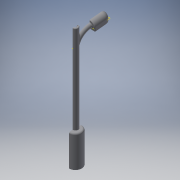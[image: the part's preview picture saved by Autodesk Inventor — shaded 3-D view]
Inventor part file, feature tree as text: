
AUTODESK INVENTOR PART (.ipt)
format: ipt  version: 2018 (Build 220112000, 112)  size: 398,336 bytes
history: native  units: in
note: dims shown in document units (in); Inventor stores cm internally (conversion verified against a paired STEP export)
features: sketch x10, other x3, plane x1
ambient origin geometry x8: Origin, YZ Plane, XZ Plane, XY Plane, X Axis, Y Axis, Z Axis, Center Point
bodies: Solid1 (feature_tree)
feature tree (14):
  other  "lampa.ipt"
  other  "Solid1::lampa.ipt"
  other  "TaggingFeature1"
  sketch  "Sketch1"  dims[d0=0.3937in]
  sketch  "Sketch6"
  sketch  "Sketch8"
  sketch  "Sketch9"
  sketch  "Sketch10"
  sketch  "Sketch11"
  sketch  "Sketch12"
  sketch  "Sketch13"
  sketch  "Sketch14"
  sketch  "Sketch15"
  plane  "Work Plane1"
